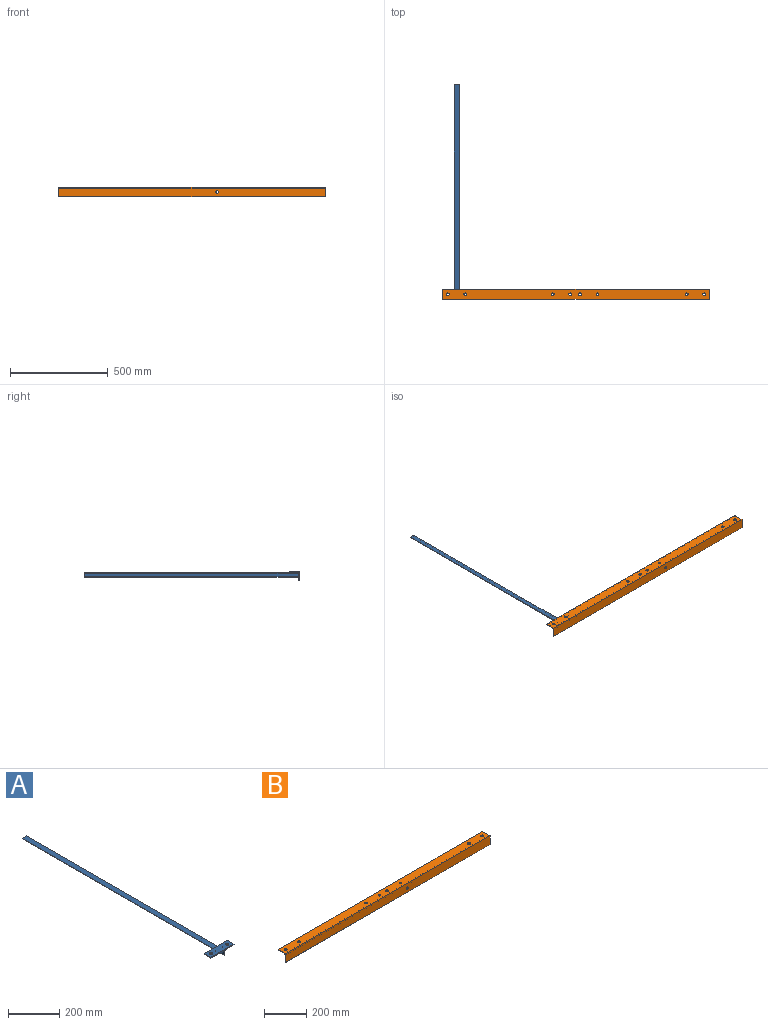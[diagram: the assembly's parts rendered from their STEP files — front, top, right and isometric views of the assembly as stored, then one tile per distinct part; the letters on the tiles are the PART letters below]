
ASSEMBLY  parts=2 mates=1
PART A: 21 faces, bbox 127x1091.7x28.6 mm
  f0: plane 127x28.58mm, normal (0,-1,0), area 562mm2, adj f1,f2,f3,f5,f6,f7,f8,f9
  f1: cylinder r=4.76mm len=1091.66mm, axis (0,1,0), area 8167.3mm2, adj f0,f2,f7,f18
  f2: plane 1091.66x14.29mm, normal (0,0,-1), area 15597mm2, adj f0,f1,f3,f18
  f3: cylinder r=3.17mm len=1091.66mm, axis (0,1,0), area 5364.7mm2, adj f0,f2,f4,f10,f15,f18
  f4: plane 1053.56x25.4mm, normal (0,0,1), area 26760.3mm2, adj f3,f5,f10,f18
  f5: plane 1091.66x25.4mm, normal (1,0,0), area 27534.5mm2, adj f0,f4,f6,f10,f14,f18
  f6: cylinder r=3.17mm len=1091.66mm, axis (0,1,0), area 5444.9mm2, adj f0,f5,f7,f18
  f7: plane 1091.66x14.29mm, normal (-1,0,0), area 15597mm2, adj f0,f1,f6,f18
  f8: plane 45.72x38.1mm, normal (0,0,-1), area 1596.5mm2, adj f0,f9,f10,f14,f17,f20
  f9: plane 38.1x3.18mm, normal (1,0,0), area 121mm2, adj f0,f8,f10,f12
  f10: plane 127x8.26mm, normal (0,1,0), area 410.2mm2, adj f3,f4,f5,f8,f9,f11,f12,f13
  f11: plane 38.1x3.18mm, normal (-1,0,0), area 121mm2, adj f0,f10,f12,f13
  f12: plane 127x38.1mm, normal (0,0,1), area 4547.8mm2, adj f0,f9,f10,f11,f16,f17,f19,f20
  f13: plane 47.47x38.1mm, normal (0,0,-1), area 1663.1mm2, adj f0,f10,f11,f15,f16,f19
  f14: cylinder r=5.08mm len=38.1mm, axis (0,1,0), area 304mm2, adj f0,f5,f8,f10
  f15: cylinder r=5.08mm len=38.1mm, axis (0,1,0), area 175.7mm2, adj f0,f3,f10,f13
  f16: cylinder r=6.75mm len=13.49mm, axis (0,0,1), area 134.6mm2, adj f12,f13
  f17: cylinder r=6.75mm len=13.49mm, axis (0,0,1), area 134.6mm2, adj f8,f12
  f18: plane 25.4x25.4mm, normal (0,1,0), area 151.7mm2, adj f1,f2,f3,f4,f5,f6,f7
  f19: cylinder r=0.89mm len=3.18mm, axis (0,0,-1), area 17.7mm2, adj f12,f13
  f20: cylinder r=0.89mm len=3.18mm, axis (0,0,-1), area 17.7mm2, adj f8,f12
PART B: 18 faces, bbox 1362.1x50.8x50.8 mm
  f0: plane 50.8x50.8mm, normal (-1,0,0), area 313mm2, adj f1,f2,f3,f4,f5,f6,f7
  f1: plane 1362.15x50.8mm, normal (0,-1,0), area 69054.2mm2, adj f0,f2,f7,f10,f17
  f2: cylinder r=3.17mm len=1362.15mm, axis (1,0,0), area 6794mm2, adj f0,f1,f3,f10
  f3: plane 1362.15x39.69mm, normal (0,1,0), area 53917.3mm2, adj f0,f2,f4,f10,f17
  f4: cylinder r=4.76mm len=1362.15mm, axis (1,0,0), area 10191mm2, adj f0,f3,f5,f10
  f5: plane 1362.15x39.69mm, normal (0,0,-1), area 52916.5mm2, adj f0,f4,f6,f8,f9,f10,f11,f12
  f6: cylinder r=3.17mm len=1362.15mm, axis (1,0,0), area 6794mm2, adj f0,f5,f7,f10
  f7: plane 1362.15x50.8mm, normal (0,0,1), area 68053.4mm2, adj f0,f1,f6,f8,f9,f10,f11,f12
  f8: cylinder r=6.75mm len=13.49mm, axis (0,0,1), area 134.6mm2, adj f5,f7
  f9: cylinder r=6.75mm len=13.49mm, axis (0,0,1), area 134.6mm2, adj f5,f7
  f10: plane 50.8x50.8mm, normal (1,0,0), area 313mm2, adj f1,f2,f3,f4,f5,f6,f7
  f11: cylinder r=6.75mm len=13.49mm, axis (0,0,1), area 134.6mm2, adj f5,f7
  f12: cylinder r=6.75mm len=13.49mm, axis (0,0,1), area 134.6mm2, adj f5,f7
  f13: cylinder r=6.75mm len=13.49mm, axis (0,0,1), area 134.6mm2, adj f5,f7
  f14: cylinder r=6.75mm len=13.49mm, axis (0,0,1), area 134.6mm2, adj f5,f7
  f15: cylinder r=6.75mm len=13.49mm, axis (0,0,1), area 134.6mm2, adj f5,f7
  f16: cylinder r=6.75mm len=13.49mm, axis (0,0,1), area 134.6mm2, adj f5,f7
  f17: cylinder r=6.75mm len=13.49mm, axis (0,-1,0), area 134.6mm2, adj f1,f3
PLACE A t=(25.67,16.91,6.44)mm
PLACE B t=(-3.82,10.56,12.79)mm
MATE fastened A.f17 <-> B.f8  axis (0,0,1) through (57.42,35.96,9.62)mm
